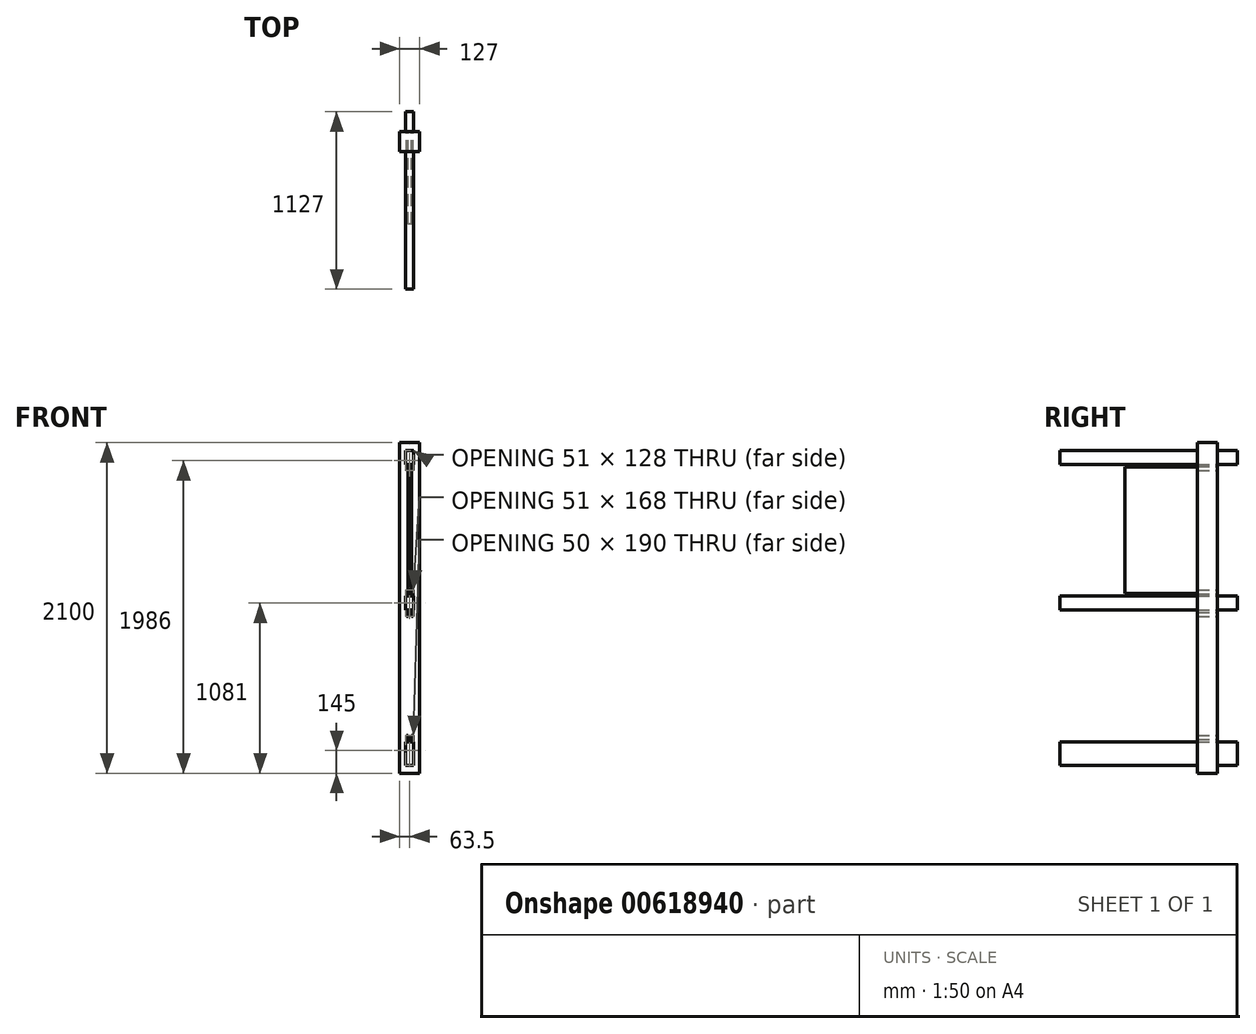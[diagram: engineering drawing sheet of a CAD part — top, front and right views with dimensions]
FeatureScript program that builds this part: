
annotation { "Feature Type Name" : "Feature", "Feature Type Description" : "" }
export const myFeature = defineFeature(function(context is Context, id is Id, definition is map)
    precondition{}
    {
        {
            var Q0;
            Q0=qCreatedBy(makeId("Front.planeOp"),FACE);
            var sketch = newSketch(context, id + "F0", { "sketchPlane" : qUnion([Q0])});
            skLineSegment(sketch, "E0.bottom", {"start": v(63.5, -1050) * mm, "end": v(-63.5, -1050) * mm});
            skLineSegment(sketch, "E0.top", {"start": v(63.5, 1050) * mm, "end": v(-63.5, 1050) * mm});
            skLineSegment(sketch, "E0.left", {"start": v(63.5, -1050) * mm, "end": v(63.5, 1050) * mm});
            skLineSegment(sketch, "E0.right", {"start": v(-63.5, -1050) * mm, "end": v(-63.5, 1050) * mm});
            skPoint(sketch, "E0.middle", {"position": v(0, 0) * mm});
            skLineSegment(sketch, "E1.bottom", {"start": v(25.5, 912) * mm, "end": v(-25.5, 912) * mm});
            skLineSegment(sketch, "E1.top", {"start": v(25.5, 1000) * mm, "end": v(-25.5, 1000) * mm});
            skLineSegment(sketch, "E1.left", {"start": v(25.5, 912) * mm, "end": v(25.5, 1000) * mm});
            skLineSegment(sketch, "E1.right", {"start": v(-25.5, 912) * mm, "end": v(-25.5, 1000) * mm});
            skPoint(sketch, "E1.middle", {"position": v(0, 956) * mm});
            skLineSegment(sketch, "E2.bottom", {"start": v(25, -1000) * mm, "end": v(-25, -1000) * mm});
            skLineSegment(sketch, "E2.top", {"start": v(25, -850) * mm, "end": v(-25, -850) * mm});
            skLineSegment(sketch, "E2.left", {"start": v(25, -1000) * mm, "end": v(25, -850) * mm});
            skLineSegment(sketch, "E2.right", {"start": v(-25, -1000) * mm, "end": v(-25, -850) * mm});
            skPoint(sketch, "E2.middle", {"position": v(0, -925) * mm});
            skLineSegment(sketch, "E3.bottom", {"start": v(25.5, -13) * mm, "end": v(-25.5, -13) * mm});
            skLineSegment(sketch, "E3.top", {"start": v(25.5, 75) * mm, "end": v(-25.5, 75) * mm});
            skLineSegment(sketch, "E3.left", {"start": v(25.5, -13) * mm, "end": v(25.5, 75) * mm});
            skLineSegment(sketch, "E3.right", {"start": v(-25.5, -13) * mm, "end": v(-25.5, 75) * mm});
            skPoint(sketch, "E3.middle", {"position": v(0, 31) * mm});
            skLineSegment(sketch, "E4.bottom", {"start": v(-20.6, -13) * mm, "end": v(21.4, -13) * mm});
            skLineSegment(sketch, "E4.left", {"start": v(-20.6, -13) * mm, "end": v(-20.6, -53) * mm});
            skLineSegment(sketch, "E4.right", {"start": v(21.4, -13) * mm, "end": v(21.4, -53) * mm});
            skLineSegment(sketch, "E5.top", {"start": v(-10.73, -28) * mm, "end": v(11.53, -28) * mm});
            skLineSegment(sketch, "E5.left", {"start": v(-10.73, -53) * mm, "end": v(-10.73, -28) * mm});
            skLineSegment(sketch, "E5.right", {"start": v(11.53, -53) * mm, "end": v(11.53, -28) * mm});
            skLineSegment(sketch, "E6.trimOffspring", {"start": v(11.53, -53) * mm, "end": v(21.4, -53) * mm});
            skLineSegment(sketch, "E7", {"start": v(-10.73, -53) * mm, "end": v(-20.6, -53) * mm});
            skLineSegment(sketch, "E8.bottom", {"start": v(-21, 912) * mm, "end": v(21, 912) * mm});
            skLineSegment(sketch, "E8.left", {"start": v(-21, 912) * mm, "end": v(-21, 872) * mm});
            skLineSegment(sketch, "E8.right", {"start": v(21, 912) * mm, "end": v(21, 872) * mm});
            skLineSegment(sketch, "E9.top", {"start": v(-11.13, 897) * mm, "end": v(11.13, 897) * mm});
            skLineSegment(sketch, "E9.left", {"start": v(-11.13, 872) * mm, "end": v(-11.13, 897) * mm});
            skLineSegment(sketch, "E9.right", {"start": v(11.13, 872) * mm, "end": v(11.13, 897) * mm});
            skLineSegment(sketch, "E10.trimOffspring", {"start": v(11.13, 872) * mm, "end": v(21, 872) * mm});
            skLineSegment(sketch, "E11", {"start": v(-11.13, 872) * mm, "end": v(-21, 872) * mm});
            skLineSegment(sketch, "E12.bottom", {"start": v(20.55, 75) * mm, "end": v(-21.45, 75) * mm});
            skLineSegment(sketch, "E12.left", {"start": v(20.55, 75) * mm, "end": v(20.55, 115) * mm});
            skLineSegment(sketch, "E12.right", {"start": v(-21.45, 75) * mm, "end": v(-21.45, 115) * mm});
            skLineSegment(sketch, "E13.top", {"start": v(10.68, 90) * mm, "end": v(-11.57, 90) * mm});
            skLineSegment(sketch, "E13.left", {"start": v(10.68, 115) * mm, "end": v(10.68, 90) * mm});
            skLineSegment(sketch, "E13.right", {"start": v(-11.57, 115) * mm, "end": v(-11.57, 90) * mm});
            skLineSegment(sketch, "E14.trimOffspring", {"start": v(-11.57, 115) * mm, "end": v(-21.45, 115) * mm});
            skLineSegment(sketch, "E15", {"start": v(10.68, 115) * mm, "end": v(20.55, 115) * mm});
            skLineSegment(sketch, "E16.bottom", {"start": v(21.79, -850) * mm, "end": v(-20.21, -850) * mm});
            skLineSegment(sketch, "E16.left", {"start": v(21.79, -850) * mm, "end": v(21.79, -810) * mm});
            skLineSegment(sketch, "E16.right", {"start": v(-20.21, -850) * mm, "end": v(-20.21, -810) * mm});
            skLineSegment(sketch, "E17.top", {"start": v(11.91, -835) * mm, "end": v(-10.34, -835) * mm});
            skLineSegment(sketch, "E17.left", {"start": v(11.91, -810) * mm, "end": v(11.91, -835) * mm});
            skLineSegment(sketch, "E17.right", {"start": v(-10.34, -810) * mm, "end": v(-10.34, -835) * mm});
            skLineSegment(sketch, "E18.trimOffspring", {"start": v(-10.34, -810) * mm, "end": v(-20.21, -810) * mm});
            skLineSegment(sketch, "E19", {"start": v(11.91, -810) * mm, "end": v(21.79, -810) * mm});
            skLineSegment(sketch, "E20", {"start": v(0.79, -850) * mm, "end": v(0.79, -13) * mm});
            skLineSegment(sketch, "E21", {"start": v(0, 75) * mm, "end": v(0, 912) * mm});
            skLineSegment(sketch, "E22.bottom", {"start": v(10.02, 91.87) * mm, "end": v(-10.02, 91.87) * mm});
            skLineSegment(sketch, "E22.top", {"start": v(10.02, 895.13) * mm, "end": v(-10.02, 895.13) * mm});
            skLineSegment(sketch, "E22.left", {"start": v(10.02, 91.87) * mm, "end": v(10.02, 895.13) * mm});
            skLineSegment(sketch, "E22.right", {"start": v(-10.02, 91.87) * mm, "end": v(-10.02, 895.13) * mm});
            skPoint(sketch, "E22.middle", {"position": v(0, 493.5) * mm});
            skSolve(sketch);
        }
        {
            var Q0;
            Q0=makeQuery(id+"F0.imprint","IMPRINT",FACE,{"disambiguationData":[TD([[makeQuery(id+"F0.imprint","IMPRINT",EDGE,{"derivedFrom":sQuery(id+"F0.wireOp",EDGE,"E0.bottom")}),-1.0]])]});
            extrude(context, id + "F1", {"entities" : qUnion([Q0]), "depth" : 127 * mm, "offsetDistance" : 25 * mm});
        }
        {
            var Q0;
            Q0=makeQuery(id+"F0.imprint","IMPRINT",FACE,{"disambiguationData":[TD([[makeQuery(id+"F0.imprint","IMPRINT",EDGE,{"derivedFrom":sQuery(id+"F0.wireOp",EDGE,"E2.bottom")}),-1.0]])]});
            var Q1;
            Q1=makeQuery(id+"F0.imprint","IMPRINT",FACE,{"disambiguationData":[TD([[makeQuery(id+"F0.imprint","IMPRINT",EDGE,{"derivedFrom":sQuery(id+"F0.wireOp",EDGE,"E16.bottom")}),-1.0]])]});
            var Q2;
            {var subQ3=sQuery(id+"F0.wireOp",EDGE,"E3.left");Q2=makeQuery(id+"F0.imprint","IMPRINT",FACE,{"disambiguationData":[TD([[makeQuery(id+"F0.imprint","IMPRINT",EDGE,{"derivedFrom":subQ3}),1.0]])]});}
            var Q3;
            Q3=makeQuery(id+"F0.imprint","IMPRINT",FACE,{"disambiguationData":[TD([[makeQuery(id+"F0.imprint","IMPRINT",EDGE,{"derivedFrom":sQuery(id+"F0.wireOp",EDGE,"E4.bottom")}),-1.0]])]});
            var Q4;
            Q4=makeQuery(id+"F0.imprint","IMPRINT",FACE,{"disambiguationData":[TD([[makeQuery(id+"F0.imprint","IMPRINT",EDGE,{"derivedFrom":sQuery(id+"F0.wireOp",EDGE,"E12.bottom")}),-1.0]])]});
            var Q5;
            Q5=makeQuery(id+"F0.imprint","IMPRINT",FACE,{"disambiguationData":[TD([[makeQuery(id+"F0.imprint","IMPRINT",EDGE,{"derivedFrom":sQuery(id+"F0.wireOp",EDGE,"E1.top")}),1.0]])]});
            var Q6;
            Q6=makeQuery(id+"F0.imprint","IMPRINT",FACE,{"disambiguationData":[TD([[makeQuery(id+"F0.imprint","IMPRINT",EDGE,{"derivedFrom":sQuery(id+"F0.wireOp",EDGE,"E8.bottom")}),-1.0]])]});
            extrude(context, id + "F2", {"entities" : qUnion([Q0, Q1, Q2, Q3, Q4, Q5, Q6]), "operationType" : NewBodyOperationType.ADD, "oppositeDirection" : true, "depth" : 127 * mm, "offsetDistance" : 25 * mm, "hasSecondDirection" : true, "secondDirectionOppositeDirection" : false, "secondDirectionDepth" : 1000 * mm});
        }
        {
            var Q0;
            {var subQ5=sQuery(id+"F0.wireOp",EDGE,"E22.left");Q0=makeQuery(id+"F0.imprint","IMPRINT",FACE,{"disambiguationData":[TD([[makeQuery(id+"F0.imprint","IMPRINT",EDGE,{"derivedFrom":subQ5}),1.0]])]});}
            var Q1;
            {var subQ5=sQuery(id+"F0.wireOp",EDGE,"E22.right");Q1=makeQuery(id+"F0.imprint","IMPRINT",FACE,{"disambiguationData":[TD([[makeQuery(id+"F0.imprint","IMPRINT",EDGE,{"derivedFrom":subQ5}),-1.0]])]});}
            extrude(context, id + "F3", {"entities" : qUnion([Q0, Q1]), "operationType" : NewBodyOperationType.ADD, "depth" : 586 * mm, "offsetDistance" : 25 * mm});
        }
    });
